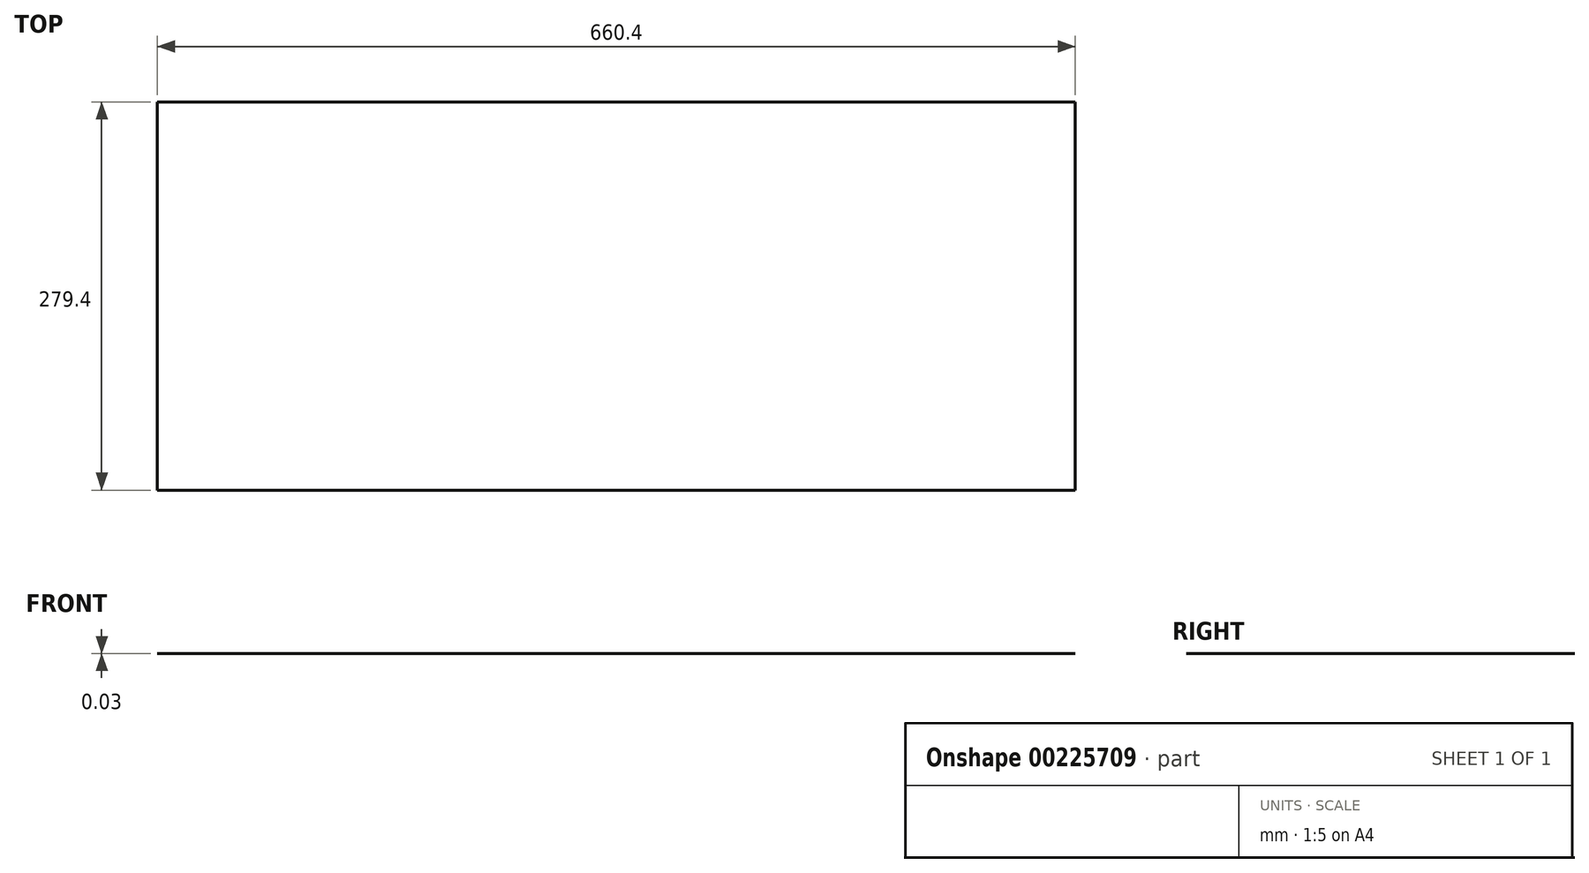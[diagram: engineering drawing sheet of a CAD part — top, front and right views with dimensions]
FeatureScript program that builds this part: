
annotation { "Feature Type Name" : "Feature", "Feature Type Description" : "" }
export const myFeature = defineFeature(function(context is Context, id is Id, definition is map)
    precondition{}
    {
        {
            var Q0;
            Q0=qCreatedBy(makeId("Top.planeOp"),FACE);
            var sketch = newSketch(context, id + "F0", { "sketchPlane" : qUnion([Q0])});
            skLineSegment(sketch, "E0.bottom", {"start": v(-300.21, 145.99) * mm, "end": v(360.19, 145.99) * mm});
            skLineSegment(sketch, "E0.top", {"start": v(-300.21, -133.41) * mm, "end": v(360.19, -133.41) * mm});
            skLineSegment(sketch, "E0.left", {"start": v(-300.21, 145.99) * mm, "end": v(-300.21, -133.41) * mm});
            skLineSegment(sketch, "E0.right", {"start": v(360.19, 145.99) * mm, "end": v(360.19, -133.41) * mm});
            skSolve(sketch);
        }
        {
            var Q0;
            Q0 = qSketchRegion(id + "F0", true);
            extrude(context, id + "F1", {"entities" : qUnion([Q0]), "depth" : 23 / 812.8 * mm});
        }
    });
